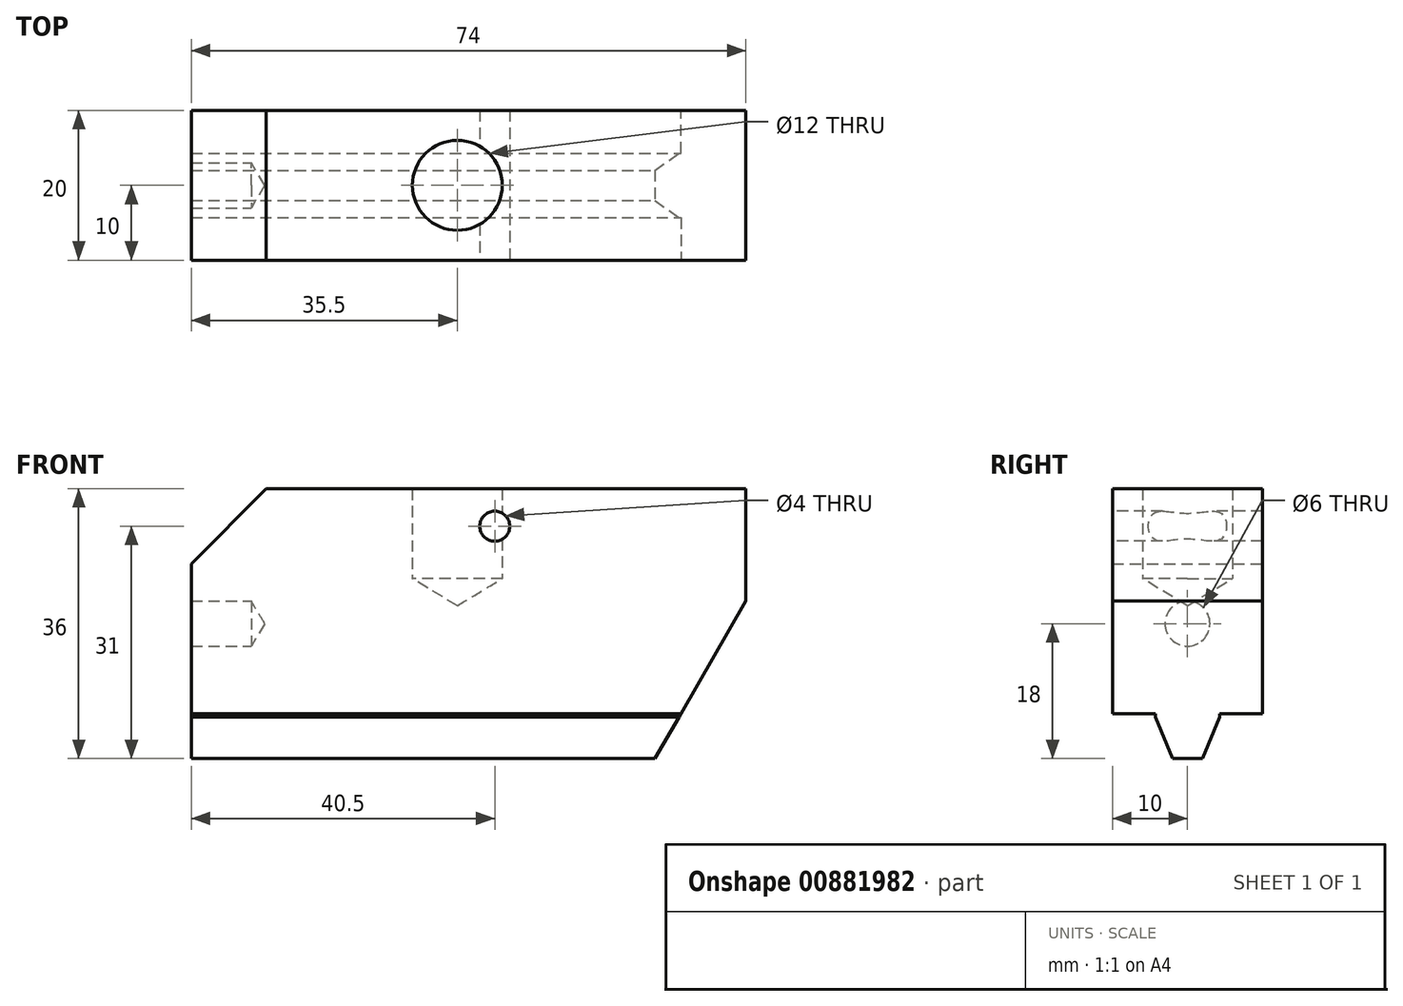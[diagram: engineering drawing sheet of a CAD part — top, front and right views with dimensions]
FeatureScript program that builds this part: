
annotation { "Feature Type Name" : "Feature", "Feature Type Description" : "" }
export const myFeature = defineFeature(function(context is Context, id is Id, definition is map)
    precondition{}
    {
        {
            var Q0;
            Q0=qCreatedBy(makeId("Front.planeOp"),FACE);
            var sketch = newSketch(context, id + "F0", { "sketchPlane" : qUnion([Q0])});
            skLineSegment(sketch, "E0", {"start": v(0, 0) * mm, "end": v(-200, 0) * mm});
            skLineSegment(sketch, "E1", {"start": v(-200, 0) * mm, "end": v(-200, 30) * mm});
            skLineSegment(sketch, "E2", {"start": v(-200, 30) * mm, "end": v(-90, 185) * mm});
            skLineSegment(sketch, "E3", {"start": v(-90, 185) * mm, "end": v(0, 185) * mm});
            skLineSegment(sketch, "E4", {"start": v(0, 185) * mm, "end": v(0, 155) * mm});
            skLineSegment(sketch, "E5", {"start": v(0, 155) * mm, "end": v(-63, 155) * mm});
            skLineSegment(sketch, "E6", {"start": v(-63, 155) * mm, "end": v(-63, 40) * mm});
            skLineSegment(sketch, "E7", {"start": v(-63, 40) * mm, "end": v(0, 40) * mm});
            skLineSegment(sketch, "E8", {"start": v(0, 40) * mm, "end": v(0, 0) * mm});
            skSolve(sketch);
        }
        {
            var Q0;
            Q0=qSketchRegion(id+"F0",true);
            extrude(context, id + "F1", {"entities" : qUnion([Q0]), "depth" : 23 * mm, "offsetDistance" : 25 * mm, "symmetric" : true});
        }
        {
            var Q0;
            Q0=makeQuery(id+"F1.opExtrude","SWEPT_FACE",FACE,{"disambiguationData":[OSD([sQuery(id+"F0.wireOp",EDGE,"E6")])]});
            var sketch = newSketch(context, id + "F2", { "sketchPlane" : qUnion([Q0])});
            skLineSegment(sketch, "E9", {"start": v(0, 135) * mm, "end": v(0, 67) * mm});
            skArc(sketch, "E10.0.startCap", {"start": v(-3.5, 135) * mm, "mid": v(0, 138.5) * mm, "end": v(3.5, 135) * mm});
            skArc(sketch, "E10.0.endCap", {"start": v(3.5, 67) * mm, "mid": v(0, 63.5) * mm, "end": v(-3.5, 67) * mm});
            skLineSegment(sketch, "E10.0.left", {"start": v(3.5, 135) * mm, "end": v(3.5, 67) * mm});
            skLineSegment(sketch, "E10.0.right", {"start": v(-3.5, 135) * mm, "end": v(-3.5, 67) * mm});
            skSolve(sketch);
        }
        {
            var Q0;
            Q0=qSketchRegion(id+"F2",true);
            extrude(context, id + "F3", {"entities" : qUnion([Q0]), "operationType" : NewBodyOperationType.REMOVE, "oppositeDirection" : true, "depth" : 5 * mm, "offsetDistance" : 25 * mm});
        }
        {
            var Q0;
            Q0=makeQuery(id+"F1.opExtrude","SWEPT_FACE",FACE,{"disambiguationData":[OSD([sQuery(id+"F0.wireOp",EDGE,"E3")])]});
            var sketch = newSketch(context, id + "F4", { "sketchPlane" : qUnion([Q0])});
            skPoint(sketch, "E11", {"position": v(-20, 0) * mm});
            skLineSegment(sketch, "E12", {"start": v(-20, 0) * mm, "end": v(0, 0) * mm, "construction": true});
            skSolve(sketch);
        }
        {
            var Q0;
            Q0=sQuery(id+"F4.wireOp",VERTEX,"E11");
            var Q1;
            Q1=makeQuery(id+"F1.opExtrude","SWEPT_BODY",BODY,{"disambiguationData":[OSD([sQuery(id+"F0.wireOp",EDGE,"E0"),sQuery(id+"F0.wireOp",EDGE,"E1"),sQuery(id+"F0.wireOp",EDGE,"E2"),sQuery(id+"F0.wireOp",EDGE,"E3"),sQuery(id+"F0.wireOp",EDGE,"E4"),sQuery(id+"F0.wireOp",EDGE,"E5"),sQuery(id+"F0.wireOp",EDGE,"E6"),sQuery(id+"F0.wireOp",EDGE,"E7"),sQuery(id+"F0.wireOp",EDGE,"E8")])]});
            hole(context, id + "F5", {"style" : HoleStyle.SIMPLE, "endStyle" : HoleEndStyle.BLIND, "standardTappedOrClearance" : lookupTablePath({ "standard" : "ISO", "engagement" : "75%", "pitch" : "2 mm", "size" : "M16", "type" : "Tapped" }), "standardBlindInLast" : lookupTablePath({ "standard" : "ISO", "engagement" : "75%", "pitch" : "2 mm", "size" : "M16", "type" : "Tapped" }), "holeDiameter" : 14 * mm, "majorDiameter" : 16 * mm, "showTappedDepth" : true, "holeDepth" : 36 * mm, "isTappedThrough" : true, "tappedDepth" : 30 * mm, "tapClearance" : 3, "locations" : qUnion([Q0]), "scope" : qUnion([Q1]), "startStyle" : HoleStartStyle.SKETCH});
        }
        {
            var Q0;
            Q0=makeQuery(id+"F1.opExtrude","SWEPT_FACE",FACE,{"disambiguationData":[OSD([sQuery(id+"F0.wireOp",EDGE,"E0")])]});
            var sketch = newSketch(context, id + "F6", { "sketchPlane" : qUnion([Q0])});
            skLineSegment(sketch, "E13", {"start": v(-200, 0) * mm, "end": v(-175, 0) * mm, "construction": true});
            skLineSegment(sketch, "E14", {"start": v(-175, 0) * mm, "end": v(-125, 0) * mm, "construction": true});
            skLineSegment(sketch, "E15", {"start": v(-125, 0) * mm, "end": v(-75, 0) * mm, "construction": true});
            skLineSegment(sketch, "E16", {"start": v(-75, 0) * mm, "end": v(-25, 0) * mm, "construction": true});
            skLineSegment(sketch, "E17", {"start": v(-25, 0) * mm, "end": v(0, 0) * mm, "construction": true});
            skSolve(sketch);
        }
        {
            var Q0;
            Q0=sQuery(id+"F6.wireOp",VERTEX,"E13.end");
            var Q1;
            Q1=sQuery(id+"F6.wireOp",VERTEX,"E14.end");
            var Q2;
            Q2=sQuery(id+"F6.wireOp",VERTEX,"E15.end");
            var Q3;
            Q3=sQuery(id+"F6.wireOp",VERTEX,"E16.end");
            var Q4;
            Q4=makeQuery(id+"F1.opExtrude","SWEPT_BODY",BODY,{"disambiguationData":[OSD([sQuery(id+"F0.wireOp",EDGE,"E0"),sQuery(id+"F0.wireOp",EDGE,"E1"),sQuery(id+"F0.wireOp",EDGE,"E2"),sQuery(id+"F0.wireOp",EDGE,"E3"),sQuery(id+"F0.wireOp",EDGE,"E4"),sQuery(id+"F0.wireOp",EDGE,"E5"),sQuery(id+"F0.wireOp",EDGE,"E6"),sQuery(id+"F0.wireOp",EDGE,"E7"),sQuery(id+"F0.wireOp",EDGE,"E8")])]});
            hole(context, id + "F7", {"style" : HoleStyle.SIMPLE, "endStyle" : HoleEndStyle.BLIND, "standardTappedOrClearance" : lookupTablePath({ "standard" : "ISO", "engagement" : "75%", "pitch" : "1.25 mm", "size" : "M8", "type" : "Tapped" }), "standardBlindInLast" : lookupTablePath({ "standard" : "ISO", "engagement" : "75%", "pitch" : "1.25 mm", "size" : "M8", "type" : "Tapped" }), "holeDiameter" : 6.8 * mm, "majorDiameter" : 8 * mm, "showTappedDepth" : true, "holeDepth" : 17 * mm, "isTappedThrough" : true, "tappedDepth" : 12 * mm, "tapClearance" : 4, "locations" : qUnion([Q0, Q1, Q2, Q3]), "scope" : qUnion([Q4]), "startStyle" : HoleStartStyle.SKETCH});
        }
        {
            var Q0;
            Q0=makeQuery(id+"F1.opExtrude","CAP_EDGE",EDGE,{"disambiguationData":[OSD([sQuery(id+"F0.wireOp",EDGE,"E7")])],"isStart":false});
            var Q1;
            Q1=makeQuery(id+"F1.opExtrude","CAP_EDGE",EDGE,{"disambiguationData":[OSD([sQuery(id+"F0.wireOp",EDGE,"E7")])],"isStart":true});
            chamfer(context, id + "F8", {"entities" : qUnion([Q0, Q1]), "chamferType" : ChamferType.OFFSET_ANGLE, "width" : 16 * mm, "oppositeDirection" : true, "angle" : 30 * degree});
        }
        {
            var Q0;
            Q0=makeQuery(id+"F1.opExtrude","SWEPT_EDGE",EDGE,{"disambiguationData":[OSD([sQuery(id+"F0.wireOp",EDGE,"E5"),sQuery(id+"F0.wireOp",EDGE,"E6")])]});
            var Q1;
            Q1=makeQuery(id+"F1.opExtrude","SWEPT_EDGE",EDGE,{"disambiguationData":[OSD([sQuery(id+"F0.wireOp",EDGE,"E6"),sQuery(id+"F0.wireOp",EDGE,"E7")])]});
            var Q2;
            Q2=makeQuery(id+"F8.opChamfer","BLEND_EDGE",EDGE,{"blendedFrom":[makeQuery(id+"F1.opExtrude","CAP_EDGE",EDGE,{"disambiguationData":[OSD([sQuery(id+"F0.wireOp",EDGE,"E7")])],"isStart":false}),makeQuery(id+"F1.opExtrude","SWEPT_FACE",FACE,{"disambiguationData":[OSD([sQuery(id+"F0.wireOp",EDGE,"E6")])]})],"blendedInto":[makeQuery(id+"F1.opExtrude","SWEPT_FACE",FACE,{"disambiguationData":[OSD([sQuery(id+"F0.wireOp",EDGE,"E6")])]})]});
            var Q3;
            Q3=makeQuery(id+"F8.opChamfer","BLEND_EDGE",EDGE,{"blendedFrom":[makeQuery(id+"F1.opExtrude","CAP_EDGE",EDGE,{"disambiguationData":[OSD([sQuery(id+"F0.wireOp",EDGE,"E7")])],"isStart":true}),makeQuery(id+"F1.opExtrude","SWEPT_FACE",FACE,{"disambiguationData":[OSD([sQuery(id+"F0.wireOp",EDGE,"E6")])]})],"blendedInto":[makeQuery(id+"F1.opExtrude","SWEPT_FACE",FACE,{"disambiguationData":[OSD([sQuery(id+"F0.wireOp",EDGE,"E6")])]})]});
            fillet(context, id + "F9", {"entities" : qUnion([Q0, Q1, Q2, Q3]), "radius" : 16 * mm, "tangentPropagation" : true, "allowEdgeOverflow" : false});
        }
        {
            var Q0;
            Q0=qCreatedBy(makeId("Right.planeOp"),FACE);
            var sketch = newSketch(context, id + "F10", { "sketchPlane" : qUnion([Q0])});
            skLineSegment(sketch, "E18", {"start": v(0, 0) * mm, "end": v(0, 90) * mm, "construction": true});
            skLineSegment(sketch, "E19", {"start": v(0, 90) * mm, "end": v(2, 90) * mm});
            skLineSegment(sketch, "E20", {"start": v(2, 90) * mm, "end": v(4.3, 95.55) * mm});
            skLineSegment(sketch, "E21", {"start": v(4.3, 95.55) * mm, "end": v(4.3, 96) * mm});
            skLineSegment(sketch, "E22", {"start": v(4.3, 96) * mm, "end": v(10, 96) * mm});
            skLineSegment(sketch, "E23", {"start": v(10, 96) * mm, "end": v(10, 126) * mm});
            skLineSegment(sketch, "E24", {"start": v(10, 126) * mm, "end": v(0, 126) * mm});
            skLineSegment(sketch, "E25.MirrorCS", {"start": v(0, 90) * mm, "end": v(-2, 90) * mm});
            skLineSegment(sketch, "E26.MirrorCS", {"start": v(-2, 90) * mm, "end": v(-4.3, 95.55) * mm});
            skLineSegment(sketch, "E27.MirrorCS", {"start": v(-4.3, 95.55) * mm, "end": v(-4.3, 96) * mm});
            skLineSegment(sketch, "E28.MirrorCS", {"start": v(-4.3, 96) * mm, "end": v(-10, 96) * mm});
            skLineSegment(sketch, "E29.MirrorCS", {"start": v(-10, 96) * mm, "end": v(-10, 126) * mm});
            skLineSegment(sketch, "E30.MirrorCS", {"start": v(-10, 126) * mm, "end": v(0, 126) * mm});
            skSolve(sketch);
        }
        {
            var Q0;
            Q0=makeQuery(id+"F10.imprint","IMPRINT",FACE,{"disambiguationData":[TD([[makeQuery(id+"F10.imprint","IMPRINT",EDGE,{"derivedFrom":sQuery(id+"F10.wireOp",EDGE,"E19")}),1.0]])]});
            extrude(context, id + "F11", {"entities" : qUnion([Q0]), "oppositeDirection" : true, "depth" : 74 * mm, "offsetDistance" : 25 * mm});
        }
        {
            var Q0;
            Q0=makeQuery(id+"F11.opExtrude","SWEPT_FACE",FACE,{"disambiguationData":[OSD([sQuery(id+"F10.wireOp",EDGE,"E29.MirrorCS")])]});
            var sketch = newSketch(context, id + "F12", { "sketchPlane" : qUnion([Q0])});
            skLineSegment(sketch, "E31", {"start": v(0, 111) * mm, "end": v(-12.12, 90) * mm});
            skLineSegment(sketch, "E32", {"start": v(-12.12, 90) * mm, "end": v(0, 90) * mm});
            skLineSegment(sketch, "E33", {"start": v(0, 90) * mm, "end": v(0, 111) * mm});
            skSolve(sketch);
        }
        {
            var Q0;
            Q0=qSketchRegion(id+"F12",true);
            var Q1;
            Q1=makeQuery(id+"F11.opExtrude","SWEPT_FACE",FACE,{"disambiguationData":[OSD([sQuery(id+"F10.wireOp",EDGE,"E23")])]});
            extrude(context, id + "F13", {"entities" : qUnion([Q0]), "operationType" : NewBodyOperationType.REMOVE, "endBound" : BoundingType.UP_TO_SURFACE, "oppositeDirection" : true, "depth" : 25 * mm, "endBoundEntityFace" : qUnion([Q1]), "offsetDistance" : 25 * mm});
        }
        {
            var Q0;
            Q0=makeQuery(id+"F11.opExtrude","CAP_EDGE",EDGE,{"disambiguationData":[OSD([sQuery(id+"F10.wireOp",EDGE,"E24"),sQuery(id+"F10.wireOp",EDGE,"E30.MirrorCS")])],"isStart":false});
            chamfer(context, id + "F14", {"entities" : qUnion([Q0]), "chamferType" : ChamferType.OFFSET_ANGLE, "width" : 10 * mm, "oppositeDirection" : true, "angle" : 45 * degree, "tangentPropagation" : true});
        }
        {
            var Q0;
            Q0=makeQuery(id+"F11.opExtrude","SWEPT_FACE",FACE,{"disambiguationData":[OSD([sQuery(id+"F10.wireOp",EDGE,"E24"),sQuery(id+"F10.wireOp",EDGE,"E30.MirrorCS")])]});
            var sketch = newSketch(context, id + "F15", { "sketchPlane" : qUnion([Q0])});
            skPoint(sketch, "E34", {"position": v(-38.5, 0) * mm});
            skLineSegment(sketch, "E35", {"start": v(-38.5, 0) * mm, "end": v(0, 0) * mm, "construction": true});
            skSolve(sketch);
        }
        {
            var Q0;
            Q0=sQuery(id+"F15.wireOp",VERTEX,"E34");
            var Q1;
            Q1=makeQuery(id+"F11.opExtrude","SWEPT_BODY",BODY,{"disambiguationData":[OSD([sQuery(id+"F10.wireOp",EDGE,"E19"),sQuery(id+"F10.wireOp",EDGE,"E20"),sQuery(id+"F10.wireOp",EDGE,"E21"),sQuery(id+"F10.wireOp",EDGE,"E22"),sQuery(id+"F10.wireOp",EDGE,"E23"),sQuery(id+"F10.wireOp",EDGE,"E24"),sQuery(id+"F10.wireOp",EDGE,"E25.MirrorCS"),sQuery(id+"F10.wireOp",EDGE,"E26.MirrorCS"),sQuery(id+"F10.wireOp",EDGE,"E27.MirrorCS"),sQuery(id+"F10.wireOp",EDGE,"E28.MirrorCS"),sQuery(id+"F10.wireOp",EDGE,"E29.MirrorCS"),sQuery(id+"F10.wireOp",EDGE,"E30.MirrorCS")])]});
            hole(context, id + "F16", {"style" : HoleStyle.SIMPLE, "endStyle" : HoleEndStyle.BLIND, "standardTappedOrClearance" : lookupTablePath({ "standard" : "ISO", "size" : "12", "type" : "Drilled" }), "standardBlindInLast" : lookupTablePath({ "standard" : "ISO", "size" : "12", "type" : "Drilled" }), "holeDiameter" : 12 * mm, "majorDiameter" : 8 * mm, "holeDepth" : 12 * mm, "isTappedThrough" : true, "tappedDepth" : 13.25 * mm, "tapClearance" : 3, "locations" : qUnion([Q0]), "scope" : qUnion([Q1]), "startStyle" : HoleStartStyle.SKETCH});
        }
        {
            var Q0;
            Q0=makeQuery(id+"F11.opExtrude","SWEPT_FACE",FACE,{"disambiguationData":[OSD([sQuery(id+"F10.wireOp",EDGE,"E29.MirrorCS")])]});
            var sketch = newSketch(context, id + "F17", { "sketchPlane" : qUnion([Q0])});
            skCircle(sketch, "E36", {"center": v(-33.5, 121) * mm, "radius": 2 * mm});
            skSolve(sketch);
        }
        {
            var Q0;
            Q0=makeQuery(id+"F17.imprint","IMPRINT",FACE,{"disambiguationData":[TD([[makeQuery(id+"F17.imprint","IMPRINT",EDGE,{"derivedFrom":sQuery(id+"F17.wireOp",EDGE,"E36")}),1.0]])]});
            var Q1;
            Q1=makeQuery(id+"F11.opExtrude","SWEPT_FACE",FACE,{"disambiguationData":[OSD([sQuery(id+"F10.wireOp",EDGE,"E23")])]});
            extrude(context, id + "F18", {"entities" : qUnion([Q0]), "operationType" : NewBodyOperationType.REMOVE, "endBound" : BoundingType.UP_TO_SURFACE, "oppositeDirection" : true, "depth" : 25 * mm, "endBoundEntityFace" : qUnion([Q1]), "offsetDistance" : 25 * mm});
        }
        {
            var Q0;
            Q0=makeQuery(id+"F1.opExtrude","SWEPT_BODY",BODY,{"disambiguationData":[OSD([sQuery(id+"F0.wireOp",EDGE,"E0"),sQuery(id+"F0.wireOp",EDGE,"E1"),sQuery(id+"F0.wireOp",EDGE,"E2"),sQuery(id+"F0.wireOp",EDGE,"E3"),sQuery(id+"F0.wireOp",EDGE,"E4"),sQuery(id+"F0.wireOp",EDGE,"E5"),sQuery(id+"F0.wireOp",EDGE,"E6"),sQuery(id+"F0.wireOp",EDGE,"E7"),sQuery(id+"F0.wireOp",EDGE,"E8")])]});
            deleteBodies(context, id + "F19", {"entities" : qUnion([Q0])});
        }
        {
            var Q0;
            Q0=makeQuery(id+"F11.opExtrude","CAP_FACE",FACE,{"disambiguationData":[OSD([sQuery(id+"F10.wireOp",EDGE,"E19"),sQuery(id+"F10.wireOp",EDGE,"E20"),sQuery(id+"F10.wireOp",EDGE,"E21"),sQuery(id+"F10.wireOp",EDGE,"E22"),sQuery(id+"F10.wireOp",EDGE,"E23"),sQuery(id+"F10.wireOp",EDGE,"E24"),sQuery(id+"F10.wireOp",EDGE,"E25.MirrorCS"),sQuery(id+"F10.wireOp",EDGE,"E26.MirrorCS"),sQuery(id+"F10.wireOp",EDGE,"E27.MirrorCS"),sQuery(id+"F10.wireOp",EDGE,"E28.MirrorCS"),sQuery(id+"F10.wireOp",EDGE,"E29.MirrorCS"),sQuery(id+"F10.wireOp",EDGE,"E30.MirrorCS")])],"isStart":false});
            var sketch = newSketch(context, id + "F20", { "sketchPlane" : qUnion([Q0])});
            skPoint(sketch, "E37", {"position": v(0, 108) * mm});
            skLineSegment(sketch, "E38", {"start": v(0, 90) * mm, "end": v(0, 108) * mm, "construction": true});
            skLineSegment(sketch, "E39", {"start": v(0, 108) * mm, "end": v(0, 126) * mm, "construction": true});
            skSolve(sketch);
        }
        {
            var Q0;
            Q0=sQuery(id+"F20.wireOp",VERTEX,"E37");
            var Q1;
            Q1=makeQuery(id+"F11.opExtrude","SWEPT_BODY",BODY,{"disambiguationData":[OSD([sQuery(id+"F10.wireOp",EDGE,"E19"),sQuery(id+"F10.wireOp",EDGE,"E20"),sQuery(id+"F10.wireOp",EDGE,"E21"),sQuery(id+"F10.wireOp",EDGE,"E22"),sQuery(id+"F10.wireOp",EDGE,"E23"),sQuery(id+"F10.wireOp",EDGE,"E24"),sQuery(id+"F10.wireOp",EDGE,"E25.MirrorCS"),sQuery(id+"F10.wireOp",EDGE,"E26.MirrorCS"),sQuery(id+"F10.wireOp",EDGE,"E27.MirrorCS"),sQuery(id+"F10.wireOp",EDGE,"E28.MirrorCS"),sQuery(id+"F10.wireOp",EDGE,"E29.MirrorCS"),sQuery(id+"F10.wireOp",EDGE,"E30.MirrorCS")])]});
            hole(context, id + "F21", {"style" : HoleStyle.SIMPLE, "endStyle" : HoleEndStyle.BLIND, "holeDiameter" : 6 * mm, "majorDiameter" : 5 * mm, "holeDepth" : 8 * mm, "isTappedThrough" : true, "tappedDepth" : 13.25 * mm, "tapClearance" : 3, "locations" : qUnion([Q0]), "scope" : qUnion([Q1]), "startStyle" : HoleStartStyle.SKETCH});
        }
    });
